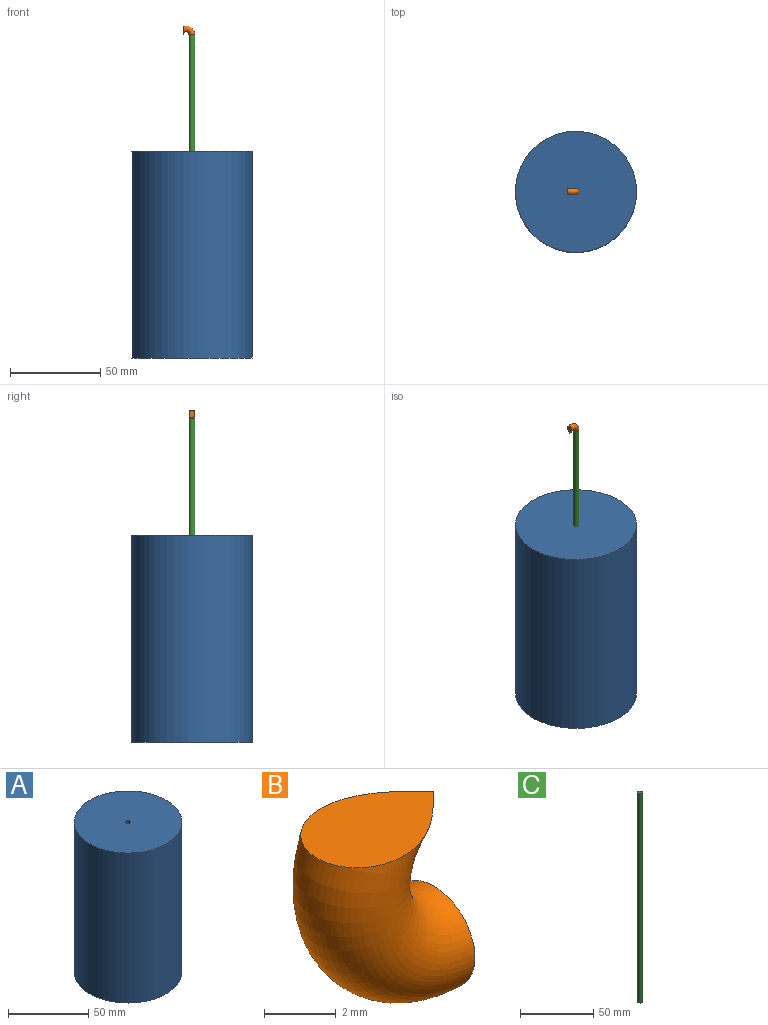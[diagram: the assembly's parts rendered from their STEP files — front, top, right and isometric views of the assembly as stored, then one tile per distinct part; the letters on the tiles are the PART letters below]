
ASSEMBLY  parts=3 mates=2
PART A: 4 faces, bbox 67.1x67.1x114.6 mm
  f0: cylinder r=1.62mm len=114.55mm, axis (0,0,-1), area 1168.6mm2, adj f2,f3
  f1: cylinder r=33.57mm len=114.55mm, axis (0,0,-1), area 24165.8mm2, adj f2,f3
  f2: plane 67.15x67.15mm, normal (0,0,1), area 3533.1mm2, adj f0,f1
  f3: plane 67.15x67.15mm, normal (0,0,-1), area 3533.1mm2, adj f0,f1
PART B: 3 faces, bbox 5.3x3.3x10.5 mm
  f0: plane 3.25x3.25mm, normal (1,0,0), area 8.3mm2, adj f1
  f1: torus R=3.24mm, axis (0,-1,0), area 70.3mm2, adj f0,f2
  f2: plane 4.59x3.25mm, normal (0,0,1), area 10.5mm2, adj f1
PART C: 3 faces, bbox 3.2x3.2x175 mm
  f0: cylinder r=1.62mm len=175.01mm, axis (0,0,-1), area 1785.3mm2, adj f1,f2
  f1: plane 3.25x3.25mm, normal (0,0,-1), area 8.3mm2, adj f0
  f2: plane 3.25x3.25mm, normal (0,0,1), area 8.3mm2, adj f0
PLACE A t=(-1.77,68.73,47.35)mm fixed
PLACE B rot(axis=(-0.71,0,0.71),180deg) t=(-5.01,68.73,159.65)mm
PLACE C t=(-47.28,20.66,51.58)mm
MATE slider C.f0 <-> A.f0  axis (0,0,-1) through (-1.77,68.73,139.08)mm
MATE revolute C.f0 <-> B.f0  axis (0,0,1) through (-1.77,68.73,226.59)mm
